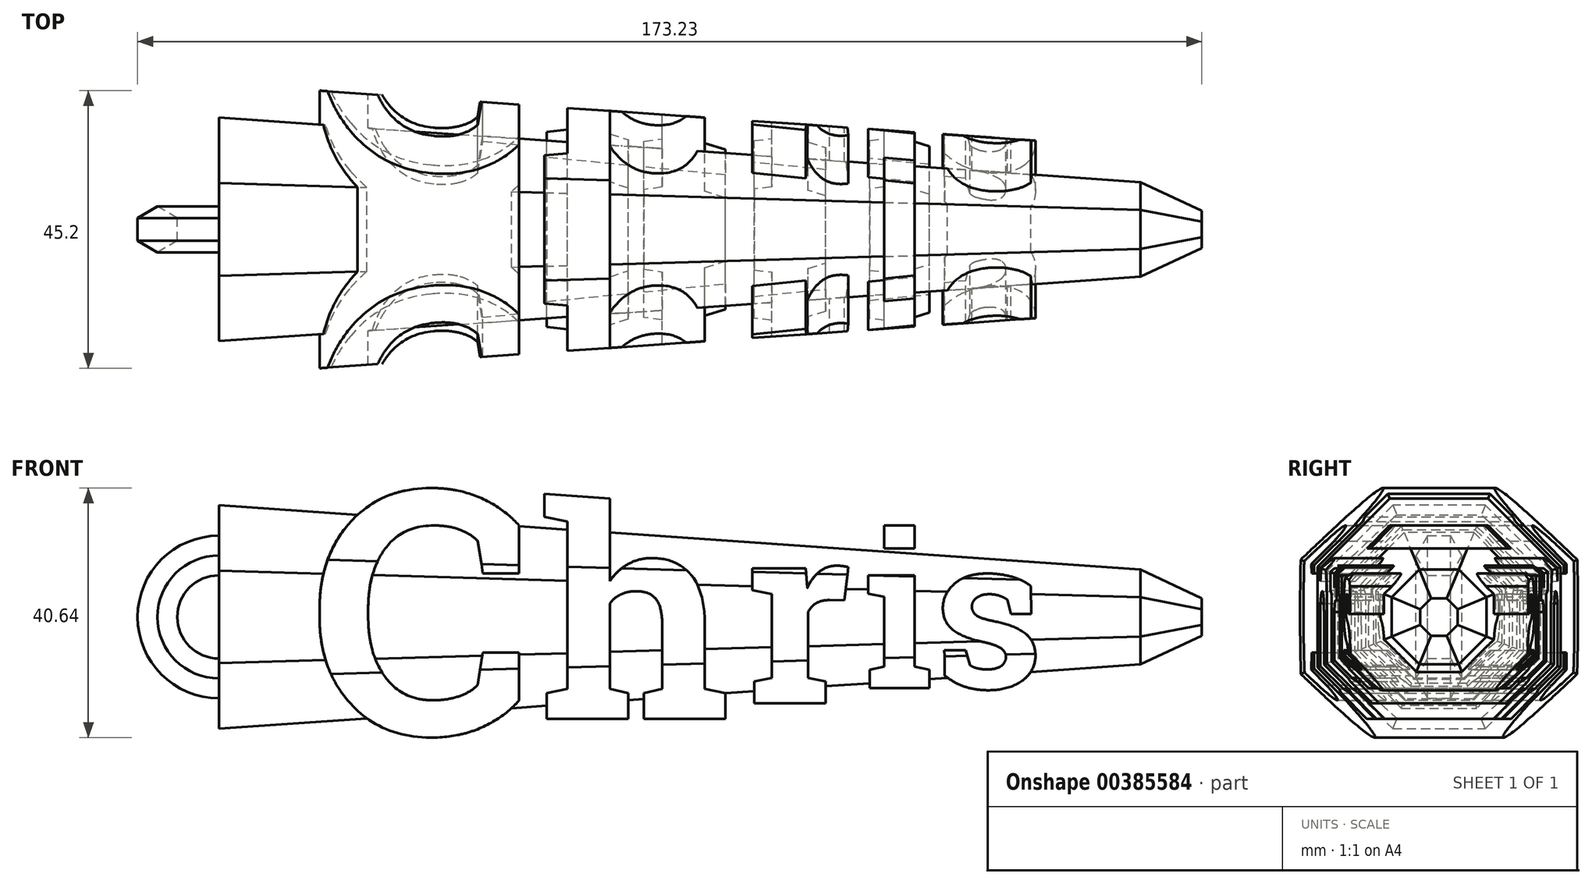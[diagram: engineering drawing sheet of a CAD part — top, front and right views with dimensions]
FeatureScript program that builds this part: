
annotation { "Feature Type Name" : "Feature", "Feature Type Description" : "" }
export const myFeature = defineFeature(function(context is Context, id is Id, definition is map)
    precondition{}
    {
        {
            assignVariable(context, id + "F0", {"name" : "hookPlane", "anyValue" : 75});
        }
        {
            assignVariable(context, id + "F1", {"name" : "halfLength", "anyValue" : 75});
        }
        {
            var Q0;
            Q0=qCreatedBy(makeId("Front.planeOp"),FACE);
            var sketch = newSketch(context, id + "F2", { "sketchPlane" : qUnion([Q0])});
            skText(sketch, "E0", { "text": "C", "fontName": "RobotoSlab-Bold.ttf"});
            skPoint(sketch, "E1", {"position": v(-22.75, 0) * mm});
            skText(sketch, "E2", { "text": "h", "fontName": "RobotoSlab-Bold.ttf"});
            skText(sketch, "E3", { "text": "r", "fontName": "RobotoSlab-Bold.ttf"});
            skText(sketch, "E4", { "text": "is", "fontName": "RobotoSlab-Bold.ttf"});
            skPoint(sketch, "E5", {"position": v(10.4, 0) * mm});
            skPoint(sketch, "E6", {"position": v(30, 0) * mm});
            skLineSegment(sketch, "E7", {"start": v(-60.03, -20) * mm, "end": v(-60.03, -51.65) * mm, "construction": true});
            skLineSegment(sketch, "E8", {"start": v(-60.03, -51.65) * mm, "end": v(60.03, -51.65) * mm, "construction": true});
            skLineSegment(sketch, "E9", {"start": v(60.03, -51.65) * mm, "end": v(60.03, -12.5) * mm, "construction": true});
            skPoint(sketch, "E10", {"position": v(0, -51.65) * mm});
            const initialGuessF2  = {"E0": [-0.06003, -0.02, 1, 0, 0.04], "E2": [-0.02275, -0.0175, 1, 0, 0.035], "E3": [0.0104, -0.015, 1, 0, 0.03], "E4": [0.03, -0.0125, 1, 0, 0.025]};
            skSetInitialGuess(sketch, initialGuessF2);
            skSolve(sketch);
        }
        {
            var Q0;
            Q0=qSketchRegion(id+"F2",true);
            extrude(context, id + "F3", {"entities" : qUnion([Q0]), "depth" : 25 * mm, "hasSecondDirection" : true, "secondDirectionOppositeDirection" : true, "secondDirectionDepth" : 25 * mm});
        }
        {
            var Q0;
            Q0=qCreatedBy(makeId("Right.planeOp"),FACE);
            var sketch = newSketch(context, id + "F4", { "sketchPlane" : qUnion([Q0])});
            skCircle(sketch, "E11", {"center": v(0, -0.93) * mm, "radius": 12.5 * mm, "construction": true});
            skCircle(sketch, "E12.cCircle", {"center": v(0, -0.93) * mm, "radius": 12.95 * mm, "construction": true});
            skLineSegment(sketch, "E12.0", {"start": v(-5.36, 12.02) * mm, "end": v(5.36, 12.02) * mm});
            skLineSegment(sketch, "E12.1", {"start": v(5.36, 12.02) * mm, "end": v(12.95, 4.43) * mm});
            skLineSegment(sketch, "E12.2", {"start": v(12.95, 4.43) * mm, "end": v(12.95, -6.3) * mm});
            skLineSegment(sketch, "E12.3", {"start": v(12.95, -6.3) * mm, "end": v(5.36, -13.88) * mm});
            skLineSegment(sketch, "E12.4", {"start": v(5.36, -13.88) * mm, "end": v(-5.36, -13.88) * mm});
            skLineSegment(sketch, "E12.5", {"start": v(-5.36, -13.88) * mm, "end": v(-12.95, -6.3) * mm});
            skLineSegment(sketch, "E12.6", {"start": v(-12.95, -6.3) * mm, "end": v(-12.95, 4.43) * mm});
            skLineSegment(sketch, "E12.7", {"start": v(-12.95, 4.43) * mm, "end": v(-5.36, 12.02) * mm});
            skPoint(sketch, "E12.0.midPoint", {"position": v(0, 12.02) * mm});
            skLineSegment(sketch, "E13", {"start": v(0, 20.07) * mm, "end": v(0, 12.02) * mm, "construction": true});
            skSolve(sketch);
        }
        {
            var Q0;
            Q0=qSketchRegion(id+"F4",true);
            var Q1;
            Q1=makeQuery(id+"F3.opExtrude","SWEPT_FACE",FACE,{"disambiguationData":[OSD([sQuery(id+"F2.wireOp",EDGE,"E4.sketch_text.stroke-1")])]});
            extrude(context, id + "F5", {"entities" : qUnion([Q0]), "operationType" : NewBodyOperationType.ADD, "oppositeDirection" : true, "depth" : (getVariable(context, 'halfLength')) * mm, "hasDraft" : true, "draftAngle" : 4 * degree, "hasSecondDirection" : true, "secondDirectionOppositeDirection" : false, "secondDirectionBoundEntityFace" : qUnion([Q1]), "secondDirectionDepth" : (getVariable(context, 'halfLength')) * mm, "hasSecondDirectionDraft" : true, "secondDirectionDraftAngle" : 4 * degree, "secondDirectionDraftPullDirection" : true});
        }
        {
            var Q0;
            Q0=qCreatedBy(makeId("Right.planeOp"),FACE);
            var sketch = newSketch(context, id + "F6", { "sketchPlane" : qUnion([Q0])});
            skCircle(sketch, "E14.cCircle", {"center": v(0, -0.93) * mm, "radius": 18.5 * mm, "construction": true});
            skLineSegment(sketch, "E14.0", {"start": v(-7.66, 17.57) * mm, "end": v(7.66, 17.57) * mm});
            skLineSegment(sketch, "E14.1", {"start": v(7.66, 17.57) * mm, "end": v(18.5, 6.73) * mm});
            skLineSegment(sketch, "E14.2", {"start": v(18.5, 6.73) * mm, "end": v(18.5, -8.6) * mm});
            skLineSegment(sketch, "E14.3", {"start": v(18.5, -8.6) * mm, "end": v(7.66, -19.43) * mm});
            skLineSegment(sketch, "E14.4", {"start": v(7.66, -19.43) * mm, "end": v(-7.66, -19.43) * mm});
            skLineSegment(sketch, "E14.5", {"start": v(-7.66, -19.43) * mm, "end": v(-18.5, -8.6) * mm});
            skLineSegment(sketch, "E14.6", {"start": v(-18.5, -8.6) * mm, "end": v(-18.5, 6.73) * mm});
            skLineSegment(sketch, "E14.7", {"start": v(-18.5, 6.73) * mm, "end": v(-7.66, 17.57) * mm});
            skLineSegment(sketch, "E15.bottom", {"start": v(37.5, 36.57) * mm, "end": v(-37.5, 36.57) * mm});
            skLineSegment(sketch, "E15.top", {"start": v(37.5, -38.43) * mm, "end": v(-37.5, -38.43) * mm});
            skLineSegment(sketch, "E15.left", {"start": v(37.5, 36.57) * mm, "end": v(37.5, -38.43) * mm});
            skLineSegment(sketch, "E15.right", {"start": v(-37.5, 36.57) * mm, "end": v(-37.5, -38.43) * mm});
            skLineSegment(sketch, "E16", {"start": v(0, 17.57) * mm, "end": v(0, 20.07) * mm, "construction": true});
            skPoint(sketch, "E16.endSnap0", {"position": v(0, 17.57) * mm});
            skSolve(sketch);
        }
        {
            var Q0;
            Q0=makeQuery(id+"F6.imprint","IMPRINT",FACE,{"disambiguationData":[TD([[makeQuery(id+"F6.imprint","IMPRINT",EDGE,{"derivedFrom":sQuery(id+"F6.wireOp",EDGE,"E14.0")}),1.0]])]});
            extrude(context, id + "F7", {"entities" : qUnion([Q0]), "operationType" : NewBodyOperationType.REMOVE, "endBound" : BoundingType.THROUGH_ALL, "depth" : 25 * mm, "hasDraft" : true, "draftAngle" : 4 * degree, "hasSecondDirection" : true, "secondDirectionBound" : SecondDirectionBoundingType.THROUGH_ALL, "secondDirectionOppositeDirection" : true, "secondDirectionDepth" : 25 * mm, "hasSecondDirectionDraft" : true, "secondDirectionDraftAngle" : 4 * degree, "secondDirectionDraftPullDirection" : true});
        }
        {
            var Q0;
            {var subQ0=sQuery(id+"F4.wireOp",EDGE,"E12.3");var subQ1=sQuery(id+"F4.wireOp",EDGE,"E12.2");var subQ2=sQuery(id+"F4.wireOp",EDGE,"E12.4");var subQ3=sQuery(id+"F4.wireOp",EDGE,"E12.5");var subQ4=sQuery(id+"F4.wireOp",EDGE,"E12.6");Q0=makeQuery(id+"F5.boolean.opBoolean","SPLIT",FACE,{"disambiguationData":[TD([makeQuery(id+"F3.opExtrude","SWEPT_FACE",FACE,{"disambiguationData":[OSD([sQuery(id+"F2.wireOp",EDGE,"E4.sketch_text.stroke-0")])]})])],"derivedFrom":makeQuery(id+"F5.opExtrude","CAP_FACE",FACE,{"disambiguationData":[OSD([sQuery(id+"F4.wireOp",EDGE,"E12.0"),sQuery(id+"F4.wireOp",EDGE,"E12.1"),subQ1,subQ0,subQ2,subQ3,subQ4,sQuery(id+"F4.wireOp",EDGE,"E12.7")])],"isStart":true})});}
            var sketch = newSketch(context, id + "F8", { "sketchPlane" : qUnion([Q0])});
            skCircle(sketch, "E17.cCircle", {"center": v(0, -0.93) * mm, "radius": 7.7 * mm, "construction": true});
            skLineSegment(sketch, "E17.0", {"start": v(-3.2, 6.77) * mm, "end": v(3.2, 6.77) * mm});
            skLineSegment(sketch, "E17.1", {"start": v(3.2, 6.77) * mm, "end": v(7.7, 2.26) * mm});
            skLineSegment(sketch, "E17.2", {"start": v(7.7, 2.26) * mm, "end": v(7.7, -4.12) * mm});
            skLineSegment(sketch, "E17.3", {"start": v(7.7, -4.12) * mm, "end": v(3.2, -8.63) * mm});
            skLineSegment(sketch, "E17.4", {"start": v(3.2, -8.63) * mm, "end": v(-3.2, -8.63) * mm});
            skLineSegment(sketch, "E17.5", {"start": v(-3.2, -8.63) * mm, "end": v(-7.7, -4.12) * mm});
            skLineSegment(sketch, "E17.6", {"start": v(-7.7, -4.12) * mm, "end": v(-7.7, 2.26) * mm});
            skLineSegment(sketch, "E17.7", {"start": v(-7.7, 2.26) * mm, "end": v(-3.2, 6.77) * mm});
            skPoint(sketch, "E17.0.midPoint", {"position": v(0, 6.77) * mm});
            skLineSegment(sketch, "E18", {"start": v(0, 19.59) * mm, "end": v(0, -20.57) * mm, "construction": true});
            skSolve(sketch);
        }
        {
            var Q0;
            Q0=qSketchRegion(id+"F8",true);
            extrude(context, id + "F9", {"entities" : qUnion([Q0]), "operationType" : NewBodyOperationType.ADD, "depth" : 10 * mm, "hasDraft" : true, "draftAngle" : 25 * degree, "draftPullDirection" : true});
        }
        {
            var Q0;
            Q0=qCreatedBy(makeId("Right.planeOp"),FACE);
            cPlane(context, id + "F10", {"entities" : qUnion([Q0]), "cplaneType" : CPlaneType.OFFSET, "offset" : (getVariable(context, 'hookPlane')) * mm, "oppositeDirection" : true, "width" : 150 * mm, "height" : 150 * mm});
        }
        {
            var Q0;
            Q0=qCreatedBy(makeId("Front.planeOp"),FACE);
            var sketch = newSketch(context, id + "F11", { "sketchPlane" : qUnion([Q0])});
            skArc(sketch, "E19", {"start": v(-68.39, 6.57) * mm, "mid": v(-85, -0.93) * mm, "end": v(-68.39, -8.43) * mm});
            skLineSegment(sketch, "E20", {"start": v(-68.39, 6.57) * mm, "end": v(-68.39, -8.43) * mm, "construction": true});
            skPoint(sketch, "E21", {"position": v(-68.39, -0.93) * mm});
            skLineSegment(sketch, "E22", {"start": v(-75, 17.26) * mm, "end": v(-75, -19.12) * mm, "construction": true});
            skSolve(sketch);
        }
        {
            var Q0;
            Q0=qCreatedBy(id+"F10.planeOp",FACE);
            var sketch = newSketch(context, id + "F12", { "sketchPlane" : qUnion([Q0])});
            skCircle(sketch, "E23.cCircle", {"center": v(0, 9.07) * mm, "radius": 3.23 * mm, "construction": true});
            skLineSegment(sketch, "E23.0", {"start": v(1.87, 5.84) * mm, "end": v(-1.87, 5.84) * mm});
            skLineSegment(sketch, "E23.1", {"start": v(-1.87, 5.84) * mm, "end": v(-3.73, 9.07) * mm});
            skLineSegment(sketch, "E23.2", {"start": v(-3.73, 9.07) * mm, "end": v(-1.87, 12.3) * mm});
            skLineSegment(sketch, "E23.3", {"start": v(-1.87, 12.3) * mm, "end": v(1.87, 12.3) * mm});
            skLineSegment(sketch, "E23.4", {"start": v(1.87, 12.3) * mm, "end": v(3.73, 9.07) * mm});
            skLineSegment(sketch, "E23.5", {"start": v(3.73, 9.07) * mm, "end": v(1.87, 5.84) * mm});
            skPoint(sketch, "E23.0.midPoint", {"position": v(0, 5.84) * mm});
            skSolve(sketch);
        }
        {
            var Q0;
            Q0=qSketchRegion(id+"F12",true);
            var Q1;
            Q1=qConstructionFilter(qBodyType(qCreatedBy(id+"F11",EDGE),BodyType.WIRE),ConstructionObject.NO);
            sweep(context, id + "F13", {"operationType" : NewBodyOperationType.ADD, "profiles" : qUnion([Q0]), "path" : qUnion([Q1])});
        }
    });
